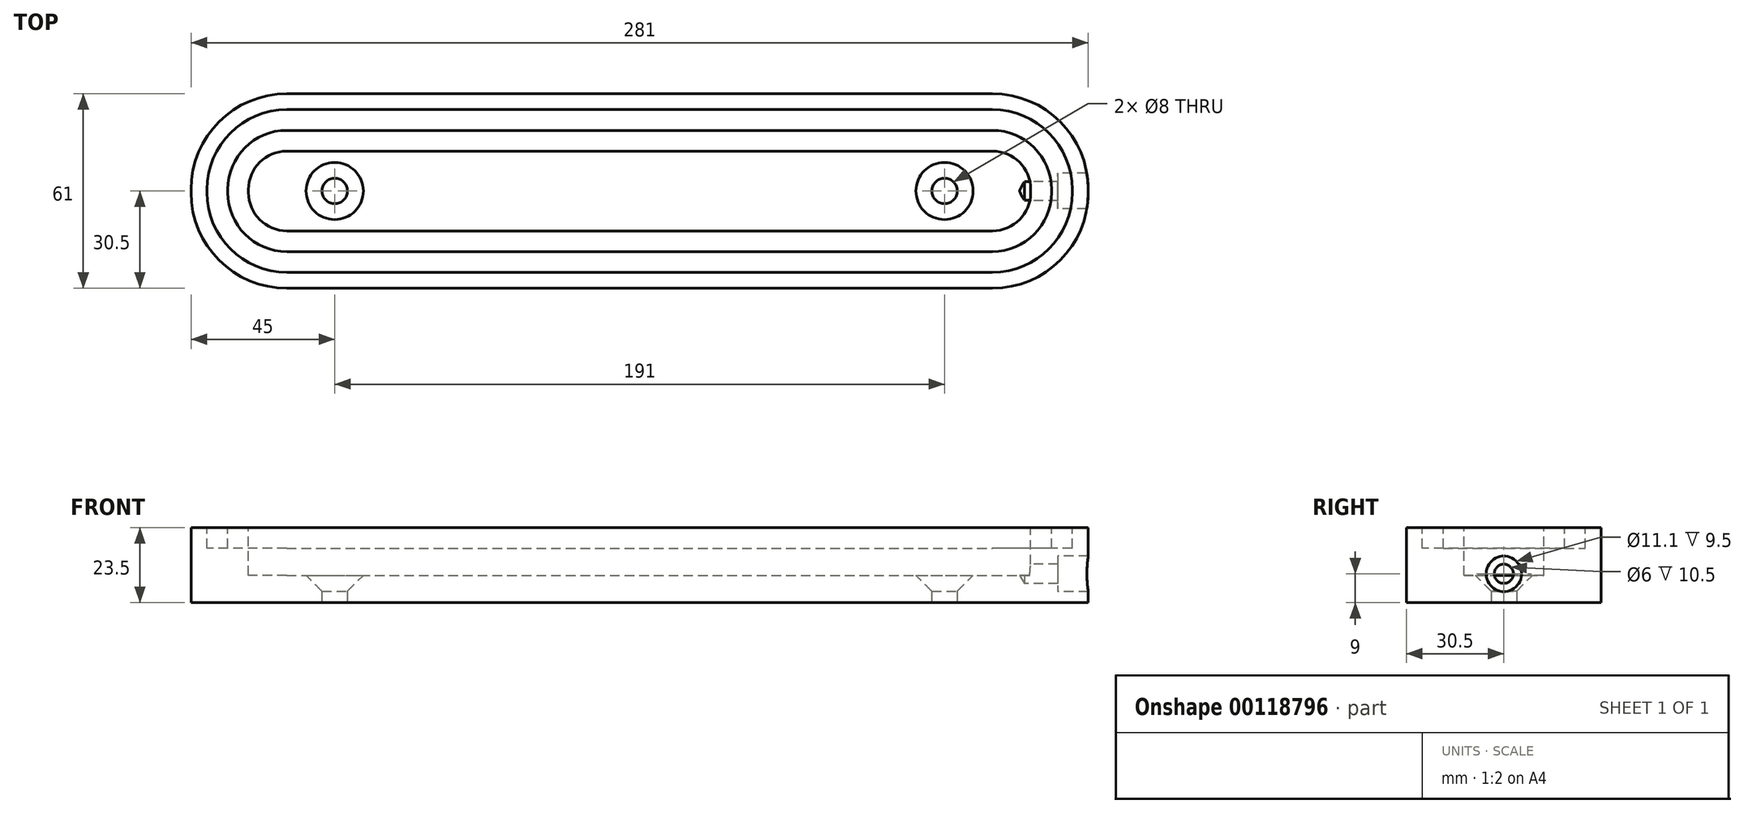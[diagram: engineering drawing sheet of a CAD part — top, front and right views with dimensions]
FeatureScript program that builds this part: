
annotation { "Feature Type Name" : "Feature", "Feature Type Description" : "" }
export const myFeature = defineFeature(function(context is Context, id is Id, definition is map)
    precondition{}
    {
        {
            assignVariable(context, id + "F0", {"name" : "thick", "anyValue" : 23.5 * mm});
        }
        {
            var Q0;
            Q0=qCreatedBy(makeId("Top.planeOp"),FACE);
            var sketch = newSketch(context, id + "F1", { "sketchPlane" : qUnion([Q0])});
            skLineSegment(sketch, "E0.bottom", {"start": v(110.5, -30.5) * mm, "end": v(-110.5, -30.5) * mm});
            skLineSegment(sketch, "E0.top", {"start": v(110.5, 30.5) * mm, "end": v(-110.5, 30.5) * mm});
            skLineSegment(sketch, "E0.left", {"start": v(140.5, -0.5) * mm, "end": v(140.5, 0.5) * mm});
            skLineSegment(sketch, "E0.right", {"start": v(-140.5, -0.5) * mm, "end": v(-140.5, 0.5) * mm});
            skPoint(sketch, "E0.middle", {"position": v(0, 0) * mm});
            skPoint(sketch, "E1.visualSharp", {"position": v(-140.5, 30.5) * mm});
            skArc(sketch, "E1.filletArc", {"start": v(-110.5, 30.5) * mm, "mid": v(-131.71, 21.71) * mm, "end": v(-140.5, 0.5) * mm});
            skPoint(sketch, "E2.visualSharp", {"position": v(-140.5, -30.5) * mm});
            skArc(sketch, "E2.filletArc", {"start": v(-140.5, -0.5) * mm, "mid": v(-131.71, -21.71) * mm, "end": v(-110.5, -30.5) * mm});
            skPoint(sketch, "E3.visualSharp", {"position": v(140.5, -30.5) * mm});
            skArc(sketch, "E3.filletArc", {"start": v(110.5, -30.5) * mm, "mid": v(131.71, -21.71) * mm, "end": v(140.5, -0.5) * mm});
            skPoint(sketch, "E4.visualSharp", {"position": v(140.5, 30.5) * mm});
            skArc(sketch, "E4.filletArc", {"start": v(140.5, 0.5) * mm, "mid": v(131.71, 21.71) * mm, "end": v(110.5, 30.5) * mm});
            skSolve(sketch);
        }
        {
            var Q0;
            Q0 = qSketchRegion(id + "F1", true);
            extrude(context, id + "F2", {"entities" : qUnion([Q0]), "depth" : getVariable(context, 'thick')});
        }
        {
            var Q0;
            Q0=makeQuery(id+"F2.opExtrude","CAP_FACE",FACE,{"disambiguationData":[OSD([sQuery(id+"F1.wireOp",EDGE,"E0.bottom"),sQuery(id+"F1.wireOp",EDGE,"E0.top"),sQuery(id+"F1.wireOp",EDGE,"E0.left"),sQuery(id+"F1.wireOp",EDGE,"E0.right"),sQuery(id+"F1.wireOp",EDGE,"E1.filletArc"),sQuery(id+"F1.wireOp",EDGE,"E2.filletArc"),sQuery(id+"F1.wireOp",EDGE,"E3.filletArc"),sQuery(id+"F1.wireOp",EDGE,"E4.filletArc")])],"isStart":false});
            var sketch = newSketch(context, id + "F3", { "sketchPlane" : qUnion([Q0])});
            skLineSegment(sketch, "E5.bottom", {"start": v(-110.5, 25.5) * mm, "end": v(110.5, 25.5) * mm});
            skLineSegment(sketch, "E5.top", {"start": v(-110.5, -25.5) * mm, "end": v(110.5, -25.5) * mm});
            skLineSegment(sketch, "E5.left", {"start": v(-135.5, 0.5) * mm, "end": v(-135.5, -0.5) * mm});
            skLineSegment(sketch, "E5.right", {"start": v(135.5, 0.5) * mm, "end": v(135.5, -0.5) * mm});
            skLineSegment(sketch, "E6.right", {"start": v(129, 0.5) * mm, "end": v(129, -0.5) * mm});
            skPoint(sketch, "E7.0", {"position": v(0, 30.5) * mm});
            skArc(sketch, "E8.0", {"start": v(140.5, 0.5) * mm, "mid": v(131.71, 21.71) * mm, "end": v(110.5, 30.5) * mm});
            skPoint(sketch, "E9.0", {"position": v(140.5, 0) * mm});
            skArc(sketch, "E10.0", {"start": v(110.5, -30.5) * mm, "mid": v(131.71, -21.71) * mm, "end": v(140.5, -0.5) * mm});
            skPoint(sketch, "E11.0", {"position": v(0, -30.5) * mm});
            skArc(sketch, "E12.0", {"start": v(-140.5, -0.5) * mm, "mid": v(-131.71, -21.71) * mm, "end": v(-110.5, -30.5) * mm});
            skPoint(sketch, "E13.0", {"position": v(-140.5, 0) * mm});
            skArc(sketch, "E14.0", {"start": v(-110.5, 30.5) * mm, "mid": v(-131.71, 21.71) * mm, "end": v(-140.5, 0.5) * mm});
            skLineSegment(sketch, "E15", {"start": v(-140.5, 0) * mm, "end": v(-135.5, 0) * mm, "construction": true});
            skLineSegment(sketch, "E16", {"start": v(0, 30.5) * mm, "end": v(0, 25.5) * mm, "construction": true});
            skLineSegment(sketch, "E17", {"start": v(0, 25.5) * mm, "end": v(0, 19) * mm, "construction": true});
            skLineSegment(sketch, "E18", {"start": v(135.5, 0) * mm, "end": v(140.5, 0) * mm, "construction": true});
            skLineSegment(sketch, "E19", {"start": v(0, -25.5) * mm, "end": v(0, -30.5) * mm, "construction": true});
            skLineSegment(sketch, "E20", {"start": v(-135.5, 0) * mm, "end": v(-129, 0) * mm, "construction": true});
            skLineSegment(sketch, "E21.trimOffspring", {"start": v(129, 0) * mm, "end": v(135.5, 0) * mm, "construction": true});
            skLineSegment(sketch, "E22.trimOffspring", {"start": v(0, -19) * mm, "end": v(0, -25.5) * mm, "construction": true});
            skArc(sketch, "E23", {"start": v(-129, 0.5) * mm, "mid": v(-123.58, 13.58) * mm, "end": v(-110.5, 19) * mm});
            skArc(sketch, "E24", {"start": v(110.5, 19) * mm, "mid": v(123.58, 13.58) * mm, "end": v(129, 0.5) * mm});
            skArc(sketch, "E25", {"start": v(129, -0.5) * mm, "mid": v(123.58, -13.58) * mm, "end": v(110.5, -19) * mm});
            skArc(sketch, "E26", {"start": v(-110.5, -19) * mm, "mid": v(-123.58, -13.58) * mm, "end": v(-129, -0.5) * mm});
            skArc(sketch, "E27", {"start": v(-135.5, 0.5) * mm, "mid": v(-128.18, 18.18) * mm, "end": v(-110.5, 25.5) * mm});
            skArc(sketch, "E28", {"start": v(110.5, 25.5) * mm, "mid": v(128.18, 18.18) * mm, "end": v(135.5, 0.5) * mm});
            skArc(sketch, "E29", {"start": v(135.5, -0.5) * mm, "mid": v(128.18, -18.18) * mm, "end": v(110.5, -25.5) * mm});
            skArc(sketch, "E30", {"start": v(-110.5, -25.5) * mm, "mid": v(-128.18, -18.18) * mm, "end": v(-135.5, -0.5) * mm});
            skLineSegment(sketch, "E31.trimOffspring", {"start": v(-110.5, 19) * mm, "end": v(110.5, 19) * mm});
            skLineSegment(sketch, "E32.trimOffspring", {"start": v(-129, 0.5) * mm, "end": v(-129, -0.5) * mm});
            skLineSegment(sketch, "E33.trimOffspring", {"start": v(-110.5, -19) * mm, "end": v(110.5, -19) * mm});
            skSolve(sketch);
        }
        {
            var Q0;
            Q0=makeQuery(id+"F3.imprint","IMPRINT",FACE,{"disambiguationData":[TD([[makeQuery(id+"F3.imprint","IMPRINT",EDGE,{"derivedFrom":sQuery(id+"F3.wireOp",EDGE,"E5.bottom")}),-1.0]])]});
            extrude(context, id + "F4", {"entities" : qUnion([Q0]), "operationType" : NewBodyOperationType.REMOVE, "oppositeDirection" : true, "depth" : 6.5 * mm});
        }
        {
            var Q0;
            Q0=makeQuery(id+"F4.boolean.opBoolean","SPLIT",FACE,{"disambiguationData":[TD([makeQuery(id+"F4.opExtrude","SWEPT_FACE",FACE,{"disambiguationData":[OSD([sQuery(id+"F3.wireOp",EDGE,"E6.right")])]})])],"derivedFrom":makeQuery(id+"F2.opExtrude","CAP_FACE",FACE,{"disambiguationData":[OSD([sQuery(id+"F1.wireOp",EDGE,"E0.bottom"),sQuery(id+"F1.wireOp",EDGE,"E0.top"),sQuery(id+"F1.wireOp",EDGE,"E0.left"),sQuery(id+"F1.wireOp",EDGE,"E0.right"),sQuery(id+"F1.wireOp",EDGE,"E1.filletArc"),sQuery(id+"F1.wireOp",EDGE,"E2.filletArc"),sQuery(id+"F1.wireOp",EDGE,"E3.filletArc"),sQuery(id+"F1.wireOp",EDGE,"E4.filletArc")])],"isStart":false})});
            var sketch = newSketch(context, id + "F5", { "sketchPlane" : qUnion([Q0])});
            skLineSegment(sketch, "E34.bottom", {"start": v(-110.5, -12.5) * mm, "end": v(110.5, -12.5) * mm});
            skLineSegment(sketch, "E34.top", {"start": v(-110.5, 12.5) * mm, "end": v(110.5, 12.5) * mm});
            skLineSegment(sketch, "E34.left", {"start": v(-122.5, -0.5) * mm, "end": v(-122.5, 0.5) * mm});
            skLineSegment(sketch, "E34.right", {"start": v(122.5, -0.5) * mm, "end": v(122.5, 0.5) * mm});
            skArc(sketch, "E35.0", {"start": v(-110.5, 30.5) * mm, "mid": v(-131.71, 21.71) * mm, "end": v(-140.5, 0.5) * mm});
            skPoint(sketch, "E36.0", {"position": v(0, 30.5) * mm});
            skArc(sketch, "E37.0", {"start": v(140.5, 0.5) * mm, "mid": v(131.71, 21.71) * mm, "end": v(110.5, 30.5) * mm});
            skPoint(sketch, "E38.0", {"position": v(140.5, 0) * mm});
            skArc(sketch, "E39.0", {"start": v(110.5, -30.5) * mm, "mid": v(131.71, -21.71) * mm, "end": v(140.5, -0.5) * mm});
            skPoint(sketch, "E40.0", {"position": v(0, -30.5) * mm});
            skArc(sketch, "E41.0", {"start": v(-140.5, -0.5) * mm, "mid": v(-131.71, -21.71) * mm, "end": v(-110.5, -30.5) * mm});
            skPoint(sketch, "E42.0", {"position": v(-140.5, 0) * mm});
            skLineSegment(sketch, "E43", {"start": v(-140.5, 0) * mm, "end": v(-122.5, 0) * mm, "construction": true});
            skLineSegment(sketch, "E44", {"start": v(0, 30.5) * mm, "end": v(0, 12.5) * mm, "construction": true});
            skLineSegment(sketch, "E45.trimOffspring", {"start": v(122.5, 0) * mm, "end": v(140.5, 0) * mm, "construction": true});
            skLineSegment(sketch, "E46.trimOffspring", {"start": v(0, -12.5) * mm, "end": v(0, -30.5) * mm, "construction": true});
            skArc(sketch, "E47", {"start": v(-122.5, 0.5) * mm, "mid": v(-118.99, 8.99) * mm, "end": v(-110.5, 12.5) * mm});
            skArc(sketch, "E48", {"start": v(-110.5, -12.5) * mm, "mid": v(-118.99, -8.99) * mm, "end": v(-122.5, -0.5) * mm});
            skArc(sketch, "E49", {"start": v(122.5, -0.5) * mm, "mid": v(118.99, -8.99) * mm, "end": v(110.5, -12.5) * mm});
            skArc(sketch, "E50", {"start": v(110.5, 12.5) * mm, "mid": v(118.99, 8.99) * mm, "end": v(122.5, 0.5) * mm});
            skSolve(sketch);
        }
        {
            var Q0;
            Q0 = qSketchRegion(id + "F5", true);
            extrude(context, id + "F6", {"entities" : qUnion([Q0]), "operationType" : NewBodyOperationType.REMOVE, "oppositeDirection" : true, "depth" : 15 * mm});
        }
        {
            var Q0;
            Q0=makeQuery(id+"F6.boolean.opBoolean","COPY",FACE,{"derivedFrom":makeQuery(id+"F6.opExtrude","CAP_FACE",FACE,{"disambiguationData":[OSD([sQuery(id+"F5.wireOp",EDGE,"E34.bottom"),sQuery(id+"F5.wireOp",EDGE,"E34.top"),sQuery(id+"F5.wireOp",EDGE,"E34.left"),sQuery(id+"F5.wireOp",EDGE,"E34.right"),sQuery(id+"F5.wireOp",EDGE,"E47"),sQuery(id+"F5.wireOp",EDGE,"E48"),sQuery(id+"F5.wireOp",EDGE,"E49"),sQuery(id+"F5.wireOp",EDGE,"E50")])],"isStart":false})});
            var sketch = newSketch(context, id + "F7", { "sketchPlane" : qUnion([Q0])});
            skLineSegment(sketch, "E51.top", {"start": v(-95.5, 0) * mm, "end": v(95.5, 0) * mm});
            skPoint(sketch, "E51.middle", {"position": v(0, 0) * mm});
            skPoint(sketch, "E52", {"position": v(95.5, 0) * mm});
            skPoint(sketch, "E53", {"position": v(-95.5, 0) * mm});
            skSolve(sketch);
        }
        {
            var Q0;
            Q0=sQuery(id+"F7.wireOp",VERTEX,"570af7c6-4feb-4633-a890-d879fe63f8d0");
            var Q1;
            Q1=sQuery(id+"F7.wireOp",VERTEX,"abcf14e7-4f44-4a98-b4f1-0b9496ebceda");
            var Q2;
            Q2=sQuery(id+"F7.wireOp",VERTEX,"E53");
            var Q3;
            Q3=sQuery(id+"F7.wireOp",VERTEX,"E52");
            var Q4;
            Q4=makeQuery(id+"F2.opExtrude","SWEPT_BODY",BODY,{"disambiguationData":[OSD([sQuery(id+"F1.wireOp",EDGE,"E0.bottom"),sQuery(id+"F1.wireOp",EDGE,"E0.top"),sQuery(id+"F1.wireOp",EDGE,"E0.left"),sQuery(id+"F1.wireOp",EDGE,"E0.right"),sQuery(id+"F1.wireOp",EDGE,"E1.filletArc"),sQuery(id+"F1.wireOp",EDGE,"E2.filletArc"),sQuery(id+"F1.wireOp",EDGE,"E3.filletArc"),sQuery(id+"F1.wireOp",EDGE,"E4.filletArc")])]});
            hole(context, id + "F8", {"style" : HoleStyle.C_SINK, "endStyle" : HoleEndStyle.THROUGH, "holeDiameter" : 8 * mm, "cSinkDiameter" : 17.92 * mm, "cSinkAngle" : 90 * degree, "tappedDepth" : 12 * mm, "tapClearance" : 3, "locations" : qUnion([Q0, Q1, Q2, Q3]), "scope" : qUnion([Q4]), "majorDiameter" : 5 * mm, "startStyle" : HoleStartStyle.SKETCH});
        }
        {
            var Q0;
            Q0=makeQuery(id+"F2.opExtrude","SWEPT_FACE",FACE,{"disambiguationData":[OSD([sQuery(id+"F1.wireOp",EDGE,"E0.left")])]});
            var sketch = newSketch(context, id + "F9", { "sketchPlane" : qUnion([Q0])});
            skPoint(sketch, "E54", {"position": v(0, 9) * mm});
            skSolve(sketch);
        }
        {
            var Q0;
            Q0=sQuery(id+"F9.wireOp",VERTEX,"E54");
            var Q1;
            Q1=makeQuery(id+"F2.opExtrude","SWEPT_BODY",BODY,{"disambiguationData":[OSD([sQuery(id+"F1.wireOp",EDGE,"E0.bottom"),sQuery(id+"F1.wireOp",EDGE,"E0.top"),sQuery(id+"F1.wireOp",EDGE,"E0.left"),sQuery(id+"F1.wireOp",EDGE,"E0.right"),sQuery(id+"F1.wireOp",EDGE,"E1.filletArc"),sQuery(id+"F1.wireOp",EDGE,"E2.filletArc"),sQuery(id+"F1.wireOp",EDGE,"E3.filletArc"),sQuery(id+"F1.wireOp",EDGE,"E4.filletArc")])]});
            hole(context, id + "F10", {"style" : HoleStyle.C_BORE, "endStyle" : HoleEndStyle.BLIND, "holeDiameter" : 6 * mm, "cBoreDiameter" : 11.1 * mm, "cBoreDepth" : 9.5 * mm, "holeDepth" : 20 * mm, "tappedDepth" : 12 * mm, "tapClearance" : 3, "locations" : qUnion([Q0]), "scope" : qUnion([Q1]), "majorDiameter" : 5 * mm, "startStyle" : HoleStartStyle.SKETCH});
        }
    });
